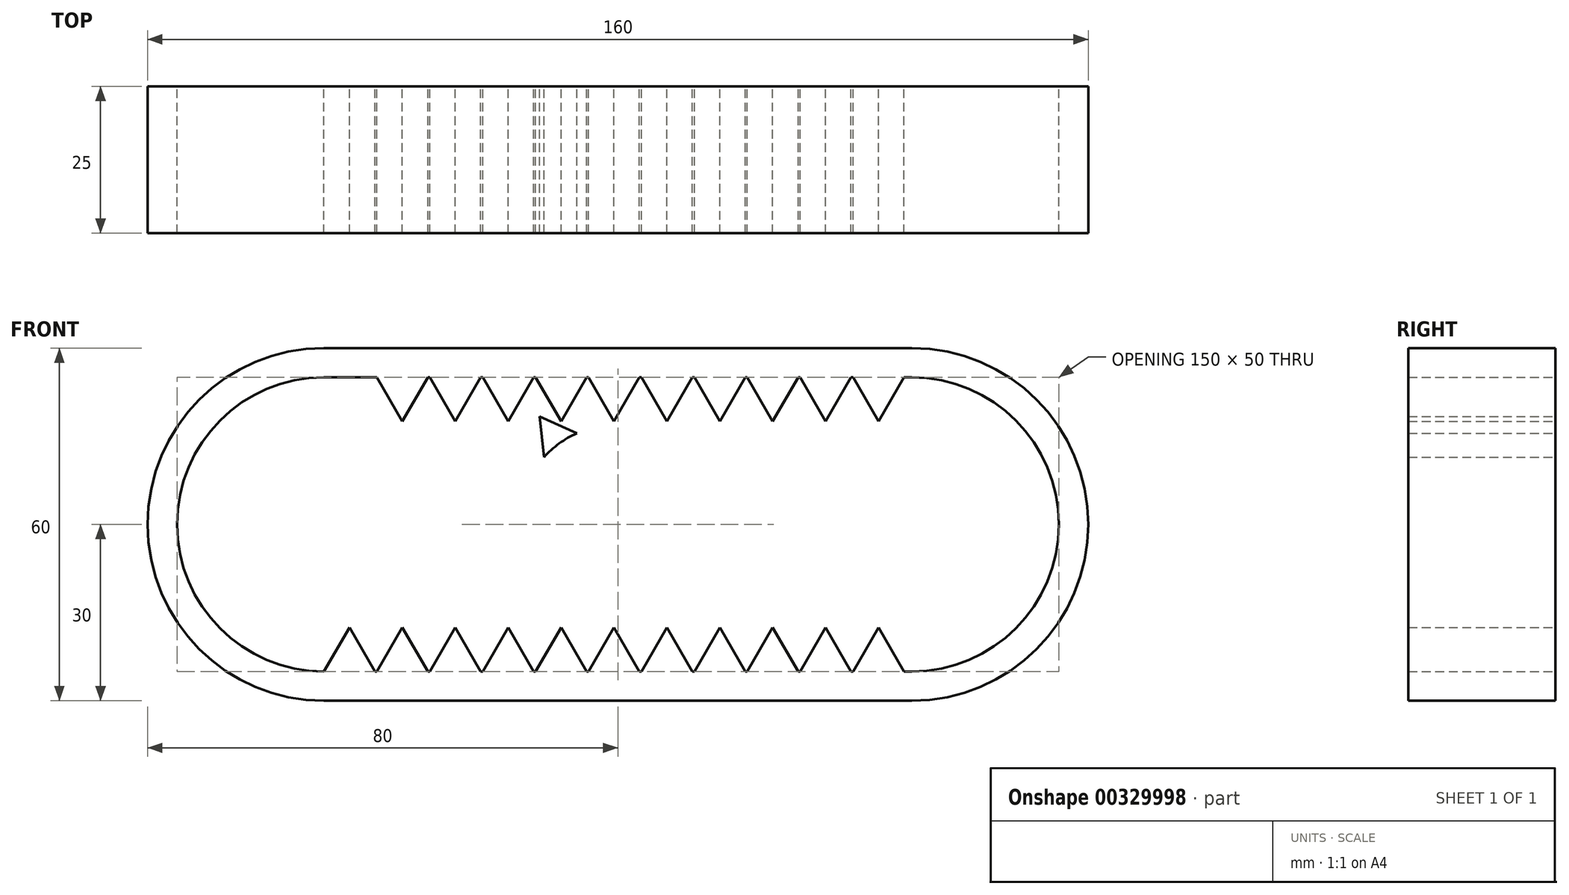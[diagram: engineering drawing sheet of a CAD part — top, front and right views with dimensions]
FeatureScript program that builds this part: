
annotation { "Feature Type Name" : "Feature", "Feature Type Description" : "" }
export const myFeature = defineFeature(function(context is Context, id is Id, definition is map)
    precondition{}
    {
        {
            var Q0;
            Q0=qCreatedBy(makeId("Front.planeOp"),FACE);
            var sketch = newSketch(context, id + "F0", { "sketchPlane" : qUnion([Q0])});
            skLineSegment(sketch, "E0.bottom", {"start": v(50, 25) * mm, "end": v(-50, 25) * mm});
            skLineSegment(sketch, "E0.top", {"start": v(50, -25) * mm, "end": v(-50, -25) * mm});
            skLineSegment(sketch, "E0.left", {"start": v(50, 25) * mm, "end": v(50, -25) * mm, "construction": true});
            skLineSegment(sketch, "E0.right", {"start": v(-50, 25) * mm, "end": v(-50, -25) * mm, "construction": true});
            skPoint(sketch, "E0.middle", {"position": v(0, 0) * mm});
            skArc(sketch, "E1", {"start": v(-50, 25) * mm, "mid": v(-75, 0) * mm, "end": v(-50, -25) * mm});
            skArc(sketch, "E2", {"start": v(50, -25) * mm, "mid": v(75, 0) * mm, "end": v(50, 25) * mm});
            skLineSegment(sketch, "E3.0", {"start": v(50, 30) * mm, "end": v(-50, 30) * mm});
            skArc(sketch, "E3.1", {"start": v(50, -30) * mm, "mid": v(80, 0) * mm, "end": v(50, 30) * mm});
            skLineSegment(sketch, "E3.2", {"start": v(50, -30) * mm, "end": v(-50, -30) * mm});
            skArc(sketch, "E3.3", {"start": v(-50, 30) * mm, "mid": v(-80, 0) * mm, "end": v(-50, -30) * mm});
            skCircle(sketch, "E4.cCircle", {"center": v(-45.67, 22.5) * mm, "radius": 2.5 * mm, "construction": true});
            skLineSegment(sketch, "E4.0", {"start": v(-50, 25) * mm, "end": v(-41.34, 25) * mm});
            skLineSegment(sketch, "E4.1", {"start": v(-41.34, 25) * mm, "end": v(-45.67, 17.5) * mm});
            skLineSegment(sketch, "E4.2", {"start": v(-45.67, 17.5) * mm, "end": v(-50, 25) * mm});
            skPoint(sketch, "E4.0.midPoint", {"position": v(-45.67, 25) * mm});
            skLineSegment(sketch, "E5.1.0.0", {"start": v(-32.34, 25) * mm, "end": v(-36.67, 17.5) * mm});
            skLineSegment(sketch, "E5.1.0.1", {"start": v(-36.67, 17.5) * mm, "end": v(-41, 25) * mm});
            skLineSegment(sketch, "E5.1.0.2", {"start": v(-41, 25) * mm, "end": v(-32.34, 25) * mm});
            skLineSegment(sketch, "E5.2.0.0", {"start": v(-23.34, 25) * mm, "end": v(-27.67, 17.5) * mm});
            skLineSegment(sketch, "E5.2.0.1", {"start": v(-27.67, 17.5) * mm, "end": v(-32, 25) * mm});
            skLineSegment(sketch, "E5.2.0.2", {"start": v(-32, 25) * mm, "end": v(-23.34, 25) * mm});
            skLineSegment(sketch, "E5.3.0.0", {"start": v(-14.34, 25) * mm, "end": v(-18.67, 17.5) * mm});
            skLineSegment(sketch, "E5.3.0.1", {"start": v(-18.67, 17.5) * mm, "end": v(-23, 25) * mm});
            skLineSegment(sketch, "E5.3.0.2", {"start": v(-23, 25) * mm, "end": v(-14.34, 25) * mm});
            skLineSegment(sketch, "E5.4.0.0", {"start": v(-5.34, 25) * mm, "end": v(-9.67, 17.5) * mm});
            skLineSegment(sketch, "E5.4.0.1", {"start": v(-9.67, 17.5) * mm, "end": v(-14, 25) * mm});
            skLineSegment(sketch, "E5.4.0.2", {"start": v(-14, 25) * mm, "end": v(-5.34, 25) * mm});
            skLineSegment(sketch, "E5.5.0.0", {"start": v(3.66, 25) * mm, "end": v(-0.67, 17.5) * mm});
            skLineSegment(sketch, "E5.5.0.1", {"start": v(-0.67, 17.5) * mm, "end": v(-5, 25) * mm});
            skLineSegment(sketch, "E5.5.0.2", {"start": v(-5, 25) * mm, "end": v(3.66, 25) * mm});
            skLineSegment(sketch, "E5.6.0.0", {"start": v(12.66, 25) * mm, "end": v(8.33, 17.5) * mm});
            skLineSegment(sketch, "E5.6.0.1", {"start": v(8.33, 17.5) * mm, "end": v(4, 25) * mm});
            skLineSegment(sketch, "E5.6.0.2", {"start": v(4, 25) * mm, "end": v(12.66, 25) * mm});
            skLineSegment(sketch, "E5.7.0.0", {"start": v(21.66, 25) * mm, "end": v(17.33, 17.5) * mm});
            skLineSegment(sketch, "E5.7.0.1", {"start": v(17.33, 17.5) * mm, "end": v(13, 25) * mm});
            skLineSegment(sketch, "E5.7.0.2", {"start": v(13, 25) * mm, "end": v(21.66, 25) * mm});
            skLineSegment(sketch, "E5.8.0.0", {"start": v(30.66, 25) * mm, "end": v(26.33, 17.5) * mm});
            skLineSegment(sketch, "E5.8.0.1", {"start": v(26.33, 17.5) * mm, "end": v(22, 25) * mm});
            skLineSegment(sketch, "E5.8.0.2", {"start": v(22, 25) * mm, "end": v(30.66, 25) * mm});
            skLineSegment(sketch, "E5.9.0.0", {"start": v(39.66, 25) * mm, "end": v(35.33, 17.5) * mm});
            skLineSegment(sketch, "E5.9.0.1", {"start": v(35.33, 17.5) * mm, "end": v(31, 25) * mm});
            skLineSegment(sketch, "E5.9.0.2", {"start": v(31, 25) * mm, "end": v(39.66, 25) * mm});
            skLineSegment(sketch, "E5.10.0.0", {"start": v(48.66, 25) * mm, "end": v(44.33, 17.5) * mm});
            skLineSegment(sketch, "E5.10.0.1", {"start": v(44.33, 17.5) * mm, "end": v(40, 25) * mm});
            skLineSegment(sketch, "E5.10.0.2", {"start": v(40, 25) * mm, "end": v(48.66, 25) * mm});
            skLineSegment(sketch, "E5.direction1", {"start": v(-45.67, 17.5) * mm, "end": v(-36.67, 17.5) * mm, "construction": true});
            skLineSegment(sketch, "E6.MirrorCS", {"start": v(-45.67, -17.5) * mm, "end": v(-50, -25) * mm});
            skLineSegment(sketch, "E7.MirrorCS", {"start": v(3.66, -25) * mm, "end": v(-0.67, -17.5) * mm});
            skLineSegment(sketch, "E8.MirrorCS", {"start": v(44.33, -17.5) * mm, "end": v(40, -25) * mm});
            skLineSegment(sketch, "E9.MirrorCS", {"start": v(-27.67, -17.5) * mm, "end": v(-32, -25) * mm});
            skLineSegment(sketch, "E10.MirrorCS", {"start": v(39.66, -25) * mm, "end": v(35.33, -17.5) * mm});
            skLineSegment(sketch, "E11.MirrorCS", {"start": v(48.66, -25) * mm, "end": v(44.33, -17.5) * mm});
            skLineSegment(sketch, "E12.MirrorCS", {"start": v(17.33, -17.5) * mm, "end": v(13, -25) * mm});
            skLineSegment(sketch, "E13.MirrorCS", {"start": v(-23.34, -25) * mm, "end": v(-27.67, -17.5) * mm});
            skLineSegment(sketch, "E14.MirrorCS", {"start": v(8.33, -17.5) * mm, "end": v(4, -25) * mm});
            skLineSegment(sketch, "E15.MirrorCS", {"start": v(-18.67, -17.5) * mm, "end": v(-23, -25) * mm});
            skLineSegment(sketch, "E16.MirrorCS", {"start": v(-9.67, -17.5) * mm, "end": v(-14, -25) * mm});
            skLineSegment(sketch, "E17.MirrorCS", {"start": v(-45.67, -17.5) * mm, "end": v(-36.67, -17.5) * mm, "construction": true});
            skLineSegment(sketch, "E18.MirrorCS", {"start": v(21.66, -25) * mm, "end": v(17.33, -17.5) * mm});
            skLineSegment(sketch, "E19.MirrorCS", {"start": v(26.33, -17.5) * mm, "end": v(22, -25) * mm});
            skLineSegment(sketch, "E20.MirrorCS", {"start": v(12.66, -25) * mm, "end": v(8.33, -17.5) * mm});
            skLineSegment(sketch, "E21.MirrorCS", {"start": v(-14.34, -25) * mm, "end": v(-18.67, -17.5) * mm});
            skLineSegment(sketch, "E22.MirrorCS", {"start": v(-5.34, -25) * mm, "end": v(-9.67, -17.5) * mm});
            skLineSegment(sketch, "E23.MirrorCS", {"start": v(35.33, -17.5) * mm, "end": v(31, -25) * mm});
            skLineSegment(sketch, "E24.MirrorCS", {"start": v(-0.67, -17.5) * mm, "end": v(-5, -25) * mm});
            skLineSegment(sketch, "E25.MirrorCS", {"start": v(-41.34, -25) * mm, "end": v(-45.67, -17.5) * mm});
            skLineSegment(sketch, "E26.MirrorCS", {"start": v(-32.34, -25) * mm, "end": v(-36.67, -17.5) * mm});
            skLineSegment(sketch, "E27.MirrorCS", {"start": v(30.66, -25) * mm, "end": v(26.33, -17.5) * mm});
            skLineSegment(sketch, "E28.MirrorCS", {"start": v(-36.67, -17.5) * mm, "end": v(-41, -25) * mm});
            skCircle(sketch, "E29.MirrorC", {"center": v(-45.67, -22.5) * mm, "radius": 2.5 * mm, "construction": true});
            skLineSegment(sketch, "E30.MirrorCS", {"start": v(-50, -25) * mm, "end": v(-50, 25) * mm, "construction": true});
            skSolve(sketch);
        }
        {
            var Q0;
            {var subQ0=sQuery(id+"F0.wireOp",EDGE,"E6.MirrorCS");Q0=makeQuery(id+"F0.imprint","IMPRINT",FACE,{"disambiguationData":[TD([[makeQuery(id+"F0.imprint","IMPRINT",EDGE,{"derivedFrom":subQ0}),1.0]])]});}
            var Q1;
            {var subQ0=sQuery(id+"F0.wireOp",EDGE,"E26.MirrorCS");Q1=makeQuery(id+"F0.imprint","IMPRINT",FACE,{"disambiguationData":[TD([[makeQuery(id+"F0.imprint","IMPRINT",EDGE,{"derivedFrom":subQ0}),1.0]])]});}
            var Q2;
            {var subQ0=sQuery(id+"F0.wireOp",EDGE,"E9.MirrorCS");Q2=makeQuery(id+"F0.imprint","IMPRINT",FACE,{"disambiguationData":[TD([[makeQuery(id+"F0.imprint","IMPRINT",EDGE,{"derivedFrom":subQ0}),1.0]])]});}
            var Q3;
            {var subQ0=sQuery(id+"F0.wireOp",EDGE,"E15.MirrorCS");Q3=makeQuery(id+"F0.imprint","IMPRINT",FACE,{"disambiguationData":[TD([[makeQuery(id+"F0.imprint","IMPRINT",EDGE,{"derivedFrom":subQ0}),1.0]])]});}
            var Q4;
            {var subQ0=sQuery(id+"F0.wireOp",EDGE,"E16.MirrorCS");Q4=makeQuery(id+"F0.imprint","IMPRINT",FACE,{"disambiguationData":[TD([[makeQuery(id+"F0.imprint","IMPRINT",EDGE,{"derivedFrom":subQ0}),1.0]])]});}
            var Q5;
            {var subQ0=sQuery(id+"F0.wireOp",EDGE,"E7.MirrorCS");Q5=makeQuery(id+"F0.imprint","IMPRINT",FACE,{"disambiguationData":[TD([[makeQuery(id+"F0.imprint","IMPRINT",EDGE,{"derivedFrom":subQ0}),1.0]])]});}
            var Q6;
            {var subQ0=sQuery(id+"F0.wireOp",EDGE,"E14.MirrorCS");Q6=makeQuery(id+"F0.imprint","IMPRINT",FACE,{"disambiguationData":[TD([[makeQuery(id+"F0.imprint","IMPRINT",EDGE,{"derivedFrom":subQ0}),1.0]])]});}
            var Q7;
            {var subQ0=sQuery(id+"F0.wireOp",EDGE,"E12.MirrorCS");Q7=makeQuery(id+"F0.imprint","IMPRINT",FACE,{"disambiguationData":[TD([[makeQuery(id+"F0.imprint","IMPRINT",EDGE,{"derivedFrom":subQ0}),1.0]])]});}
            var Q8;
            {var subQ0=sQuery(id+"F0.wireOp",EDGE,"E19.MirrorCS");Q8=makeQuery(id+"F0.imprint","IMPRINT",FACE,{"disambiguationData":[TD([[makeQuery(id+"F0.imprint","IMPRINT",EDGE,{"derivedFrom":subQ0}),1.0]])]});}
            var Q9;
            {var subQ0=sQuery(id+"F0.wireOp",EDGE,"E10.MirrorCS");Q9=makeQuery(id+"F0.imprint","IMPRINT",FACE,{"disambiguationData":[TD([[makeQuery(id+"F0.imprint","IMPRINT",EDGE,{"derivedFrom":subQ0}),1.0]])]});}
            var Q10;
            {var subQ0=sQuery(id+"F0.wireOp",EDGE,"E8.MirrorCS");Q10=makeQuery(id+"F0.imprint","IMPRINT",FACE,{"disambiguationData":[TD([[makeQuery(id+"F0.imprint","IMPRINT",EDGE,{"derivedFrom":subQ0}),1.0]])]});}
            var Q11;
            {var subQ3=sQuery(id+"F0.wireOp",EDGE,"E1");Q11=makeQuery(id+"F0.imprint","IMPRINT",FACE,{"disambiguationData":[TD([[makeQuery(id+"F0.imprint","IMPRINT",EDGE,{"derivedFrom":subQ3}),-1.0]])]});}
            var Q12;
            Q12=makeQuery(id+"F0.imprint","IMPRINT",FACE,{"disambiguationData":[TD([[makeQuery(id+"F0.imprint","IMPRINT",EDGE,{"derivedFrom":sQuery(id+"F0.wireOp",EDGE,"E4.0")}),-1.0]])]});
            var Q13;
            Q13=makeQuery(id+"F0.imprint","IMPRINT",FACE,{"disambiguationData":[TD([[makeQuery(id+"F0.imprint","IMPRINT",EDGE,{"derivedFrom":sQuery(id+"F0.wireOp",EDGE,"E5.2.0.0")}),-1.0]])]});
            var Q14;
            Q14=makeQuery(id+"F0.imprint","IMPRINT",FACE,{"disambiguationData":[TD([[makeQuery(id+"F0.imprint","IMPRINT",EDGE,{"derivedFrom":sQuery(id+"F0.wireOp",EDGE,"E5.3.0.0")}),-1.0]])]});
            var Q15;
            Q15=makeQuery(id+"F0.imprint","IMPRINT",FACE,{"disambiguationData":[TD([[makeQuery(id+"F0.imprint","IMPRINT",EDGE,{"derivedFrom":sQuery(id+"F0.wireOp",EDGE,"E5.4.0.0")}),-1.0]])]});
            var Q16;
            Q16=makeQuery(id+"F0.imprint","IMPRINT",FACE,{"disambiguationData":[TD([[makeQuery(id+"F0.imprint","IMPRINT",EDGE,{"derivedFrom":sQuery(id+"F0.wireOp",EDGE,"E5.5.0.0")}),-1.0]])]});
            var Q17;
            Q17=makeQuery(id+"F0.imprint","IMPRINT",FACE,{"disambiguationData":[TD([[makeQuery(id+"F0.imprint","IMPRINT",EDGE,{"derivedFrom":sQuery(id+"F0.wireOp",EDGE,"E5.6.0.0")}),-1.0]])]});
            var Q18;
            Q18=makeQuery(id+"F0.imprint","IMPRINT",FACE,{"disambiguationData":[TD([[makeQuery(id+"F0.imprint","IMPRINT",EDGE,{"derivedFrom":sQuery(id+"F0.wireOp",EDGE,"E5.7.0.0")}),-1.0]])]});
            var Q19;
            Q19=makeQuery(id+"F0.imprint","IMPRINT",FACE,{"disambiguationData":[TD([[makeQuery(id+"F0.imprint","IMPRINT",EDGE,{"derivedFrom":sQuery(id+"F0.wireOp",EDGE,"E5.8.0.0")}),-1.0]])]});
            var Q20;
            Q20=makeQuery(id+"F0.imprint","IMPRINT",FACE,{"disambiguationData":[TD([[makeQuery(id+"F0.imprint","IMPRINT",EDGE,{"derivedFrom":sQuery(id+"F0.wireOp",EDGE,"E5.9.0.0")}),-1.0]])]});
            var Q21;
            Q21=makeQuery(id+"F0.imprint","IMPRINT",FACE,{"disambiguationData":[TD([[makeQuery(id+"F0.imprint","IMPRINT",EDGE,{"derivedFrom":sQuery(id+"F0.wireOp",EDGE,"E5.10.0.0")}),-1.0]])]});
            var Q22;
            Q22=makeQuery(id+"F0.imprint","IMPRINT",FACE,{"disambiguationData":[TD([[makeQuery(id+"F0.imprint","IMPRINT",EDGE,{"derivedFrom":sQuery(id+"F0.wireOp",EDGE,"E5.1.0.0")}),-1.0]])]});
            extrude(context, id + "F1", {"entities" : qUnion([Q0, Q1, Q2, Q3, Q4, Q5, Q6, Q7, Q8, Q9, Q10, Q11, Q12, Q13, Q14, Q15, Q16, Q17, Q18, Q19, Q20, Q21, Q22]), "endBound" : BoundingType.SYMMETRIC, "depth" : 25 * mm});
        }
        {
            var Q0;
            Q0=qCreatedBy(makeId("Front.planeOp"),FACE);
            var sketch = newSketch(context, id + "F2", { "sketchPlane" : qUnion([Q0])});
            skArc(sketch, "E31", {"start": v(-3.46, 16.64) * mm, "mid": v(-10, 13.75) * mm, "end": v(-14.76, 8.44) * mm});
            skCircle(sketch, "E32.cCircle", {"center": v(0, 18.64) * mm, "radius": 2 * mm, "construction": true});
            skLineSegment(sketch, "E32.0", {"start": v(0, 22.64) * mm, "end": v(3.46, 16.64) * mm});
            skLineSegment(sketch, "E32.2", {"start": v(-3.46, 16.64) * mm, "end": v(0, 22.64) * mm});
            skPoint(sketch, "E32.0.midPoint", {"position": v(1.73, 19.64) * mm});
            skLineSegment(sketch, "E33", {"start": v(0, 18.64) * mm, "end": v(0, 22.64) * mm, "construction": true});
            skLineSegment(sketch, "E34.anchor1", {"start": v(0, 0) * mm, "end": v(-3.46, 16.64) * mm, "construction": true});
            skLineSegment(sketch, "E34.anchor2", {"start": v(0, 0) * mm, "end": v(-3.46, 16.64) * mm, "construction": true});
            skLineSegment(sketch, "E35.1.0", {"start": v(-13.3, 18.32) * mm, "end": v(-6.98, 15.5) * mm});
            skLineSegment(sketch, "E35.1.1", {"start": v(-12.59, 11.43) * mm, "end": v(-13.3, 18.32) * mm});
            skLineSegment(sketch, "E35.2.0", {"start": v(-21.54, 7) * mm, "end": v(-14.76, 8.44) * mm});
            skLineSegment(sketch, "E35.2.1", {"start": v(-16.9, 1.85) * mm, "end": v(-21.54, 7) * mm});
            skLineSegment(sketch, "E35.3.0", {"start": v(-21.54, -7) * mm, "end": v(-16.9, -1.85) * mm});
            skLineSegment(sketch, "E35.3.1", {"start": v(-14.76, -8.44) * mm, "end": v(-21.54, -7) * mm});
            skLineSegment(sketch, "E35.4.0", {"start": v(-13.3, -18.32) * mm, "end": v(-12.59, -11.43) * mm});
            skLineSegment(sketch, "E35.4.1", {"start": v(-6.98, -15.5) * mm, "end": v(-13.3, -18.32) * mm});
            skLineSegment(sketch, "E35.5.0", {"start": v(0, -22.64) * mm, "end": v(-3.46, -16.64) * mm});
            skLineSegment(sketch, "E35.5.1", {"start": v(3.46, -16.64) * mm, "end": v(0, -22.64) * mm});
            skLineSegment(sketch, "E35.6.0", {"start": v(13.3, -18.32) * mm, "end": v(6.98, -15.5) * mm});
            skLineSegment(sketch, "E35.6.1", {"start": v(12.59, -11.43) * mm, "end": v(13.3, -18.32) * mm});
            skLineSegment(sketch, "E35.7.0", {"start": v(21.54, -7) * mm, "end": v(14.76, -8.44) * mm});
            skLineSegment(sketch, "E35.7.1", {"start": v(16.9, -1.85) * mm, "end": v(21.54, -7) * mm});
            skLineSegment(sketch, "E35.8.0", {"start": v(21.54, 7) * mm, "end": v(16.9, 1.85) * mm});
            skLineSegment(sketch, "E35.8.1", {"start": v(14.76, 8.44) * mm, "end": v(21.54, 7) * mm});
            skLineSegment(sketch, "E35.9.0", {"start": v(13.3, 18.32) * mm, "end": v(12.59, 11.43) * mm});
            skLineSegment(sketch, "E35.9.1", {"start": v(6.98, 15.5) * mm, "end": v(13.3, 18.32) * mm});
            skArc(sketch, "E36.trimOffspring", {"start": v(-14.76, -8.44) * mm, "mid": v(-13.75, -10) * mm, "end": v(-12.59, -11.43) * mm});
            skArc(sketch, "E37.trimOffspring", {"start": v(-16.9, 1.85) * mm, "mid": v(-17, 0) * mm, "end": v(-16.9, -1.85) * mm});
            skArc(sketch, "E38.trimOffspring", {"start": v(-6.98, -15.5) * mm, "mid": v(-5.25, -16.17) * mm, "end": v(-3.46, -16.64) * mm});
            skArc(sketch, "E39.trimOffspring", {"start": v(3.46, -16.64) * mm, "mid": v(5.25, -16.17) * mm, "end": v(6.98, -15.5) * mm});
            skArc(sketch, "E40.trimOffspring", {"start": v(12.59, -11.43) * mm, "mid": v(13.75, -10) * mm, "end": v(14.76, -8.44) * mm});
            skArc(sketch, "E41.trimOffspring", {"start": v(16.9, -1.85) * mm, "mid": v(17, 0) * mm, "end": v(16.9, 1.85) * mm});
            skArc(sketch, "E42.trimOffspring", {"start": v(14.76, 8.44) * mm, "mid": v(13.75, 10) * mm, "end": v(12.59, 11.43) * mm});
            skArc(sketch, "E43.trimOffspring", {"start": v(6.98, 15.5) * mm, "mid": v(5.25, 16.17) * mm, "end": v(3.46, 16.64) * mm});
            skSolve(sketch);
        }
        {
            var Q0;
            {var subQ0=sQuery(id+"F2.wireOp",EDGE,"E32.2");Q0=makeQuery(id+"F2.imprint","IMPRINT",FACE,{"disambiguationData":[TD([[makeQuery(id+"F2.imprint","IMPRINT",EDGE,{"derivedFrom":subQ0}),-1.0]])]});}
            var Q1;
            {var subQ0=sQuery(id+"F2.wireOp",EDGE,"E35.1.0");Q1=makeQuery(id+"F2.imprint","IMPRINT",FACE,{"disambiguationData":[TD([[makeQuery(id+"F2.imprint","IMPRINT",EDGE,{"derivedFrom":subQ0}),-1.0]])]});}
            extrude(context, id + "F3", {"entities" : qUnion([Q0, Q1]), "endBound" : BoundingType.SYMMETRIC, "depth" : 25 * mm});
        }
    });
